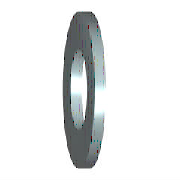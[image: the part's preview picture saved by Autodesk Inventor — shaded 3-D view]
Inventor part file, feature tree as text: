
AUTODESK INVENTOR PART (.ipt)
format: ipt  version: 2023.3 (Build 273359000, 359)  size: 106,496 bytes
history: native  units: mm (DEFAULTED — no unit token found)
features: extrude x1, other x1, plane x1, sketch x1
ambient origin geometry x7: Origin, YZ Plane, XY Plane, X Axis, Y Axis, Z Axis, Center Point
bodies: Solid1 (feature_tree)
feature tree (4):
  extrude  "Körper"  Depth=0.5mm
  other  "Work Axis1"
  plane  "Work Plane1"
  sketch  "Skizze"  dims[d0=3.4mm d1=7.0mm d2=0.5mm d3=0.0mm d4=0.0mm d5=0.0mm d6=0.0mm d7=0.0mm]
